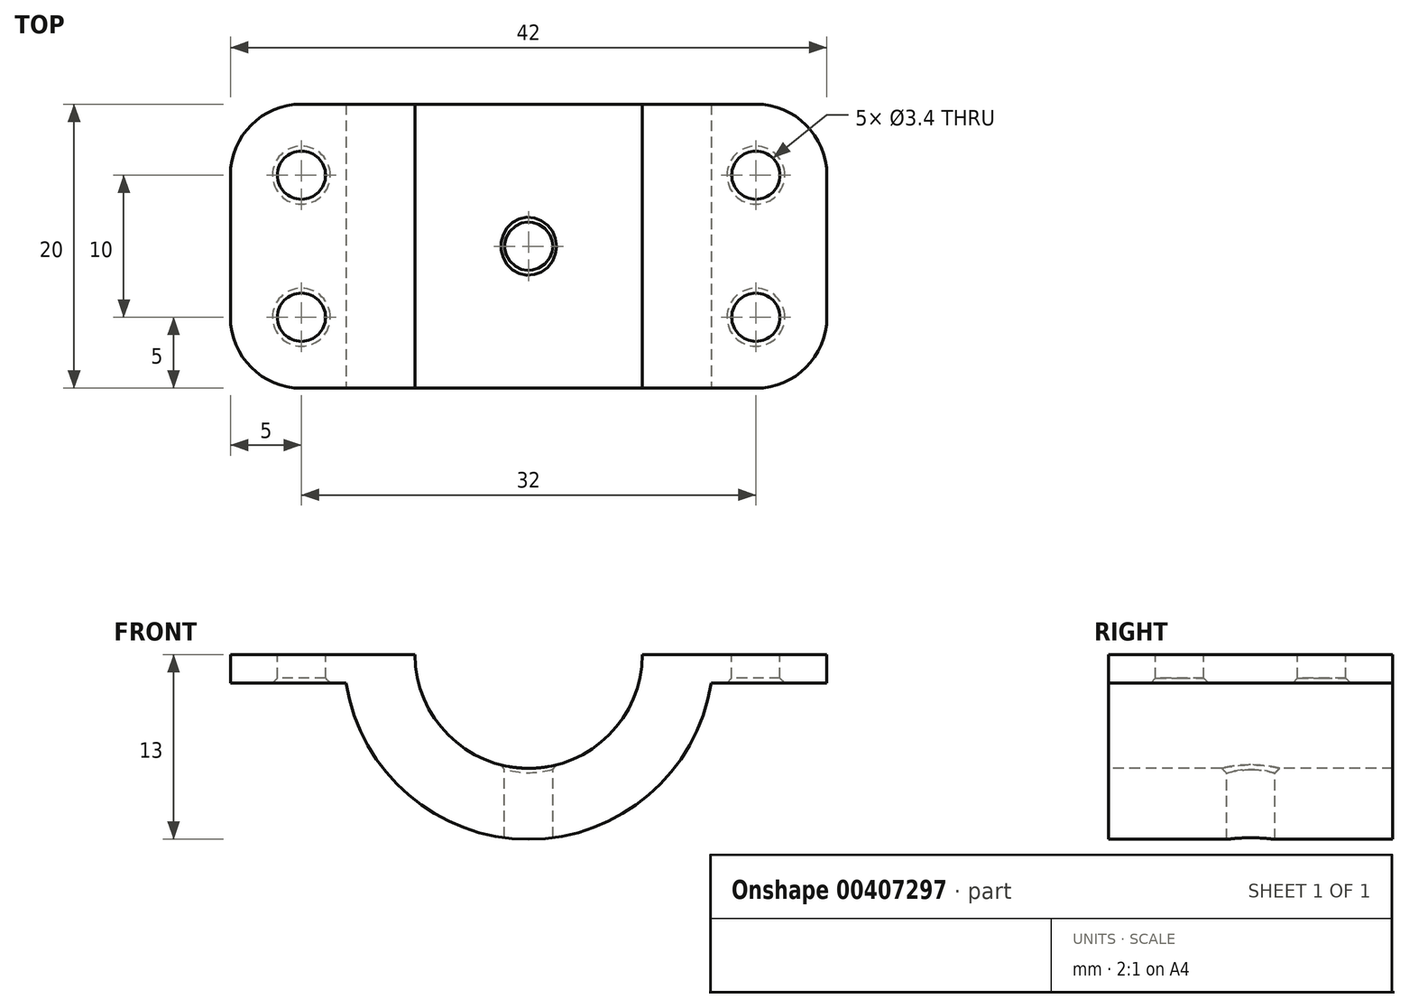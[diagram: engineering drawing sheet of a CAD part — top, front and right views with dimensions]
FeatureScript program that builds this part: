
annotation { "Feature Type Name" : "Feature", "Feature Type Description" : "" }
export const myFeature = defineFeature(function(context is Context, id is Id, definition is map)
    precondition{}
    {
        {
            var Q0;
            Q0=qCreatedBy(makeId("Top.planeOp"),FACE);
            var sketch = newSketch(context, id + "F0", { "sketchPlane" : qUnion([Q0])});
            skLineSegment(sketch, "E0.bottom", {"start": v(0, 0) * mm, "end": v(55, 0) * mm});
            skLineSegment(sketch, "E0.top", {"start": v(0, -20) * mm, "end": v(55, -20) * mm});
            skLineSegment(sketch, "E0.left", {"start": v(0, 0) * mm, "end": v(0, -20) * mm});
            skLineSegment(sketch, "E0.right", {"start": v(55, 0) * mm, "end": v(55, -20) * mm});
            skSolve(sketch);
        }
        {
            var Q0;
            Q0 = qSketchRegion(id + "F0", true);
            extrude(context, id + "F1", {"entities" : qUnion([Q0]), "depth" : 13 * mm});
        }
        {
            var Q0;
            Q0=makeQuery(id+"F1.opExtrude","SWEPT_FACE",FACE,{"disambiguationData":[OSD([sQuery(id+"F0.wireOp",EDGE,"E0.top")])]});
            var sketch = newSketch(context, id + "F2", { "sketchPlane" : qUnion([Q0])});
            skLineSegment(sketch, "E1", {"start": v(27.5, 0) * mm, "end": v(27.5, 13) * mm});
            skCircle(sketch, "E2", {"center": v(27.5, 13) * mm, "radius": 8 * mm});
            skCircle(sketch, "E3.0", {"center": v(27.5, 13) * mm, "radius": 13 * mm});
            skSolve(sketch);
        }
        {
            var Q0;
            {var subQ1=sQuery(id+"F0.wireOp",EDGE,"E0.top");var subQ6=makeQuery(id+"F1.opExtrude","SWEPT_EDGE",EDGE,{"disambiguationData":[OSD([subQ1,sQuery(id+"F0.wireOp",EDGE,"E0.left")])]});Q0=makeQuery(id+"F2.imprint","IMPRINT",FACE,{"disambiguationData":[TD([[makeQuery(id+"F2.imprint","IMPRINT",EDGE,{"derivedFrom":subQ6}),1.0]])]});}
            var Q1;
            {var subQ1=sQuery(id+"F0.wireOp",EDGE,"E0.top");var subQ6=makeQuery(id+"F1.opExtrude","SWEPT_EDGE",EDGE,{"disambiguationData":[OSD([subQ1,sQuery(id+"F0.wireOp",EDGE,"E0.right")])]});Q1=makeQuery(id+"F2.imprint","IMPRINT",FACE,{"disambiguationData":[TD([[makeQuery(id+"F2.imprint","IMPRINT",EDGE,{"derivedFrom":subQ6}),-1.0]])]});}
            var Q2;
            {var subQ0=sQuery(id+"F2.wireOp",EDGE,"E1");var subQ1=makeQuery(id+"F1.opExtrude","CAP_EDGE",EDGE,{"disambiguationData":[OSD([sQuery(id+"F0.wireOp",EDGE,"E0.top")])],"isStart":false});var subQ2=makeQuery(id+"F2.imprint","INTERSECT",VERTEX,{"derivedFrom":[subQ1,subQ0]});Q2=makeQuery(id+"F2.imprint","IMPRINT",FACE,{"disambiguationData":[TD([[makeQuery(id+"F2.imprint","IMPRINT",EDGE,{"disambiguationData":[TD([[subQ2,1.0]])],"derivedFrom":subQ0}),1.0]])]});}
            var Q3;
            {var subQ0=sQuery(id+"F2.wireOp",EDGE,"E1");var subQ1=makeQuery(id+"F1.opExtrude","CAP_EDGE",EDGE,{"disambiguationData":[OSD([sQuery(id+"F0.wireOp",EDGE,"E0.top")])],"isStart":false});var subQ2=makeQuery(id+"F2.imprint","INTERSECT",VERTEX,{"derivedFrom":[subQ1,subQ0]});Q3=makeQuery(id+"F2.imprint","IMPRINT",FACE,{"disambiguationData":[TD([[makeQuery(id+"F2.imprint","IMPRINT",EDGE,{"disambiguationData":[TD([[subQ2,1.0]])],"derivedFrom":subQ0}),-1.0]])]});}
            extrude(context, id + "F3", {"entities" : qUnion([Q0, Q1, Q2, Q3]), "operationType" : NewBodyOperationType.REMOVE, "oppositeDirection" : true, "depth" : 20 * mm});
        }
        {
            var Q0;
            Q0=makeQuery(id+"F3.boolean.opBoolean","SPLIT",FACE,{"disambiguationData":[OD(0.0)],"derivedFrom":makeQuery(id+"F1.opExtrude","CAP_FACE",FACE,{"disambiguationData":[OSD([sQuery(id+"F0.wireOp",EDGE,"E0.bottom"),sQuery(id+"F0.wireOp",EDGE,"E0.top"),sQuery(id+"F0.wireOp",EDGE,"E0.left"),sQuery(id+"F0.wireOp",EDGE,"E0.right")])],"isStart":false})});
            var sketch = newSketch(context, id + "F4", { "sketchPlane" : qUnion([Q0])});
            skPoint(sketch, "E4.oppositeSnap0", {"position": v(17, -20) * mm});
            skLineSegment(sketch, "E4.bottom", {"start": v(19.5, 0) * mm, "end": v(6.5, 0) * mm});
            skLineSegment(sketch, "E4.top", {"start": v(19.5, -20) * mm, "end": v(6.5, -20) * mm});
            skLineSegment(sketch, "E4.left", {"start": v(19.5, 0) * mm, "end": v(19.5, -20) * mm});
            skLineSegment(sketch, "E4.right", {"start": v(6.5, 0) * mm, "end": v(6.5, -20) * mm});
            skLineSegment(sketch, "E5", {"start": v(19.5, 0) * mm, "end": v(35.5, 0) * mm});
            skLineSegment(sketch, "E6.bottom", {"start": v(35.5, 0) * mm, "end": v(48.5, 0) * mm});
            skLineSegment(sketch, "E6.top", {"start": v(35.5, -20) * mm, "end": v(48.5, -20) * mm});
            skLineSegment(sketch, "E6.left", {"start": v(35.5, 0) * mm, "end": v(35.5, -20) * mm});
            skLineSegment(sketch, "E6.right", {"start": v(48.5, 0) * mm, "end": v(48.5, -20) * mm});
            skSolve(sketch);
        }
        {
            var Q0;
            Q0 = qSketchRegion(id + "F4", true);
            extrude(context, id + "F5", {"entities" : qUnion([Q0]), "operationType" : NewBodyOperationType.ADD, "oppositeDirection" : true, "depth" : 2 * mm});
        }
        {
            var Q0;
            Q0=makeQuery(id+"F5.opExtrude","SWEPT_EDGE",EDGE,{"disambiguationData":[OSD([sQuery(id+"F4.wireOp",EDGE,"E4.top"),sQuery(id+"F4.wireOp",EDGE,"E4.right")])]});
            var Q1;
            Q1=makeQuery(id+"F5.opExtrude","SWEPT_EDGE",EDGE,{"disambiguationData":[OSD([sQuery(id+"F4.wireOp",EDGE,"E4.bottom"),sQuery(id+"F4.wireOp",EDGE,"E4.right")])]});
            var Q2;
            Q2=makeQuery(id+"F5.opExtrude","SWEPT_EDGE",EDGE,{"disambiguationData":[OSD([sQuery(id+"F4.wireOp",EDGE,"E6.top"),sQuery(id+"F4.wireOp",EDGE,"E6.right")])]});
            var Q3;
            Q3=makeQuery(id+"F5.opExtrude","SWEPT_EDGE",EDGE,{"disambiguationData":[OSD([sQuery(id+"F4.wireOp",EDGE,"E6.bottom"),sQuery(id+"F4.wireOp",EDGE,"E6.right")])]});
            fillet(context, id + "F6", {"entities" : qUnion([Q0, Q1, Q2, Q3]), "radius" : 5 * mm, "tangentPropagation" : true, "allowEdgeOverflow" : false});
        }
        {
            var Q0;
            Q0=makeQuery(id+"F5.boolean.opBoolean","MERGE",FACE,{"derivedFrom":[makeQuery(id+"F3.boolean.opBoolean","SPLIT",FACE,{"disambiguationData":[OD(0.0)],"derivedFrom":makeQuery(id+"F1.opExtrude","CAP_FACE",FACE,{"disambiguationData":[OSD([sQuery(id+"F0.wireOp",EDGE,"E0.bottom"),sQuery(id+"F0.wireOp",EDGE,"E0.top"),sQuery(id+"F0.wireOp",EDGE,"E0.left"),sQuery(id+"F0.wireOp",EDGE,"E0.right")])],"isStart":false})}),makeQuery(id+"F5.opExtrude","CAP_FACE",FACE,{"disambiguationData":[OSD([sQuery(id+"F4.wireOp",EDGE,"E4.bottom"),sQuery(id+"F4.wireOp",EDGE,"E4.top"),sQuery(id+"F4.wireOp",EDGE,"E4.left"),sQuery(id+"F4.wireOp",EDGE,"E4.right")])],"isStart":true})]});
            var sketch = newSketch(context, id + "F7", { "sketchPlane" : qUnion([Q0])});
            skLineSegment(sketch, "E7", {"start": v(6.5, -10) * mm, "end": v(11.5, -10) * mm});
            skLineSegment(sketch, "E8", {"start": v(11.5, -10) * mm, "end": v(11.5, -5) * mm});
            skLineSegment(sketch, "E9", {"start": v(11.5, -5) * mm, "end": v(11.5, -15) * mm});
            skCircle(sketch, "E10", {"center": v(11.5, -5) * mm, "radius": 1.7 * mm});
            skCircle(sketch, "E11", {"center": v(11.5, -15) * mm, "radius": 1.7 * mm});
            skLineSegment(sketch, "E12", {"start": v(0, 0) * mm, "end": v(27.5, 0) * mm});
            skLineSegment(sketch, "E13", {"start": v(27.5, 0) * mm, "end": v(27.5, -10) * mm});
            skLineSegment(sketch, "E14.MirrorCS", {"start": v(43.5, -10) * mm, "end": v(43.5, -5) * mm});
            skLineSegment(sketch, "E15.MirrorCS", {"start": v(48.5, -10) * mm, "end": v(43.5, -10) * mm});
            skLineSegment(sketch, "E16.MirrorCS", {"start": v(43.5, -5) * mm, "end": v(43.5, -15) * mm});
            skCircle(sketch, "E17.MirrorC", {"center": v(43.5, -5) * mm, "radius": 1.7 * mm});
            skCircle(sketch, "E18.MirrorC", {"center": v(43.5, -15) * mm, "radius": 1.7 * mm});
            skCircle(sketch, "E19", {"center": v(27.5, -10) * mm, "radius": 1.7 * mm});
            skSolve(sketch);
        }
        {
            var Q0;
            Q0 = qSketchRegion(id + "F7", true);
            extrude(context, id + "F8", {"entities" : qUnion([Q0]), "operationType" : NewBodyOperationType.REMOVE, "oppositeDirection" : true, "depth" : 25 * mm});
        }
        {
            var Q0;
            Q0=makeQuery(id+"F8.boolean.opBoolean","COPY",EDGE,{"derivedFrom":makeQuery(id+"F8.opExtrude","CAP_EDGE",EDGE,{"disambiguationData":[OSD([sQuery(id+"F7.wireOp",EDGE,"E10")])],"isStart":true})});
            var Q1;
            Q1=makeQuery(id+"F8.boolean.opBoolean","INTERSECT",EDGE,{"derivedFrom":[makeQuery(id+"F5.opExtrude","CAP_FACE",FACE,{"disambiguationData":[OSD([sQuery(id+"F4.wireOp",EDGE,"E4.bottom"),sQuery(id+"F4.wireOp",EDGE,"E4.top"),sQuery(id+"F4.wireOp",EDGE,"E4.left"),sQuery(id+"F4.wireOp",EDGE,"E4.right")])],"isStart":false}),makeQuery(id+"F8.opExtrude","SWEPT_FACE",FACE,{"disambiguationData":[OSD([sQuery(id+"F7.wireOp",EDGE,"E10")])]})]});
            var Q2;
            Q2=makeQuery(id+"F8.boolean.opBoolean","COPY",EDGE,{"derivedFrom":makeQuery(id+"F8.opExtrude","CAP_EDGE",EDGE,{"disambiguationData":[OSD([sQuery(id+"F7.wireOp",EDGE,"E11")])],"isStart":true})});
            var Q3;
            Q3=makeQuery(id+"F8.boolean.opBoolean","INTERSECT",EDGE,{"derivedFrom":[makeQuery(id+"F5.opExtrude","CAP_FACE",FACE,{"disambiguationData":[OSD([sQuery(id+"F4.wireOp",EDGE,"E4.bottom"),sQuery(id+"F4.wireOp",EDGE,"E4.top"),sQuery(id+"F4.wireOp",EDGE,"E4.left"),sQuery(id+"F4.wireOp",EDGE,"E4.right")])],"isStart":false}),makeQuery(id+"F8.opExtrude","SWEPT_FACE",FACE,{"disambiguationData":[OSD([sQuery(id+"F7.wireOp",EDGE,"E11")])]})]});
            var Q4;
            Q4=makeQuery(id+"F8.boolean.opBoolean","COPY",EDGE,{"derivedFrom":makeQuery(id+"F8.opExtrude","CAP_EDGE",EDGE,{"disambiguationData":[OSD([sQuery(id+"F7.wireOp",EDGE,"E18.MirrorC")])],"isStart":true})});
            var Q5;
            Q5=makeQuery(id+"F8.boolean.opBoolean","INTERSECT",EDGE,{"derivedFrom":[makeQuery(id+"F5.opExtrude","CAP_FACE",FACE,{"disambiguationData":[OSD([sQuery(id+"F4.wireOp",EDGE,"E6.bottom"),sQuery(id+"F4.wireOp",EDGE,"E6.top"),sQuery(id+"F4.wireOp",EDGE,"E6.left"),sQuery(id+"F4.wireOp",EDGE,"E6.right")])],"isStart":false}),makeQuery(id+"F8.opExtrude","SWEPT_FACE",FACE,{"disambiguationData":[OSD([sQuery(id+"F7.wireOp",EDGE,"E18.MirrorC")])]})]});
            var Q6;
            Q6=makeQuery(id+"F8.boolean.opBoolean","COPY",EDGE,{"derivedFrom":makeQuery(id+"F8.opExtrude","CAP_EDGE",EDGE,{"disambiguationData":[OSD([sQuery(id+"F7.wireOp",EDGE,"E17.MirrorC")])],"isStart":true})});
            var Q7;
            Q7=makeQuery(id+"F8.boolean.opBoolean","INTERSECT",EDGE,{"derivedFrom":[makeQuery(id+"F5.opExtrude","CAP_FACE",FACE,{"disambiguationData":[OSD([sQuery(id+"F4.wireOp",EDGE,"E6.bottom"),sQuery(id+"F4.wireOp",EDGE,"E6.top"),sQuery(id+"F4.wireOp",EDGE,"E6.left"),sQuery(id+"F4.wireOp",EDGE,"E6.right")])],"isStart":false}),makeQuery(id+"F8.opExtrude","SWEPT_FACE",FACE,{"disambiguationData":[OSD([sQuery(id+"F7.wireOp",EDGE,"E17.MirrorC")])]})]});
            var Q8;
            Q8=makeQuery(id+"F8.boolean.opBoolean","INTERSECT",EDGE,{"derivedFrom":[makeQuery(id+"F3.boolean.opBoolean","COPY",FACE,{"derivedFrom":makeQuery(id+"F3.opExtrude","SWEPT_FACE",FACE,{"disambiguationData":[OSD([sQuery(id+"F2.wireOp",EDGE,"E2")])]})}),makeQuery(id+"F8.opExtrude","SWEPT_FACE",FACE,{"disambiguationData":[OSD([sQuery(id+"F7.wireOp",EDGE,"E19")])]})]});
            var Q9;
            {var subQ0=sQuery(id+"F2.wireOp",EDGE,"E3.0");var subQ1=sQuery(id+"F0.wireOp",EDGE,"E0.top");var subQ3=makeQuery(id+"F1.opExtrude","CAP_EDGE",EDGE,{"disambiguationData":[OSD([subQ1])],"isStart":false});Q9=makeQuery(id+"F8.boolean.opBoolean","INTERSECT",EDGE,{"derivedFrom":[makeQuery(id+"F3.boolean.opBoolean","TWEAK_FACE",FACE,{"derivedFrom":[makeQuery(id+"F3.opExtrude","SWEPT_FACE",FACE,{"disambiguationData":[OSD([subQ0]),TDD([makeQuery(id+"F2.imprint","IMPRINT",EDGE,{"disambiguationData":[TD([[makeQuery(id+"F2.imprint","INTERSECT",VERTEX,{"disambiguationData":[OD(0.0)],"derivedFrom":[subQ3,subQ0]}),-1.0]])],"derivedFrom":subQ0})])]}),makeQuery(id+"F3.opExtrude","SWEPT_FACE",FACE,{"disambiguationData":[OSD([subQ0]),TDD([makeQuery(id+"F2.imprint","IMPRINT",EDGE,{"disambiguationData":[TD([[makeQuery(id+"F2.imprint","INTERSECT",VERTEX,{"disambiguationData":[OD(1.0)],"derivedFrom":[subQ3,subQ0]}),1.0]])],"derivedFrom":subQ0})])]})]}),makeQuery(id+"F8.opExtrude","SWEPT_FACE",FACE,{"disambiguationData":[OSD([sQuery(id+"F7.wireOp",EDGE,"E19")])]})]});}
            chamfer(context, id + "F9", {"entities" : qUnion([Q0, Q1, Q2, Q3, Q4, Q5, Q6, Q7, Q8, Q9]), "width" : 0.34 * mm, "tangentPropagation" : true});
        }
    });
